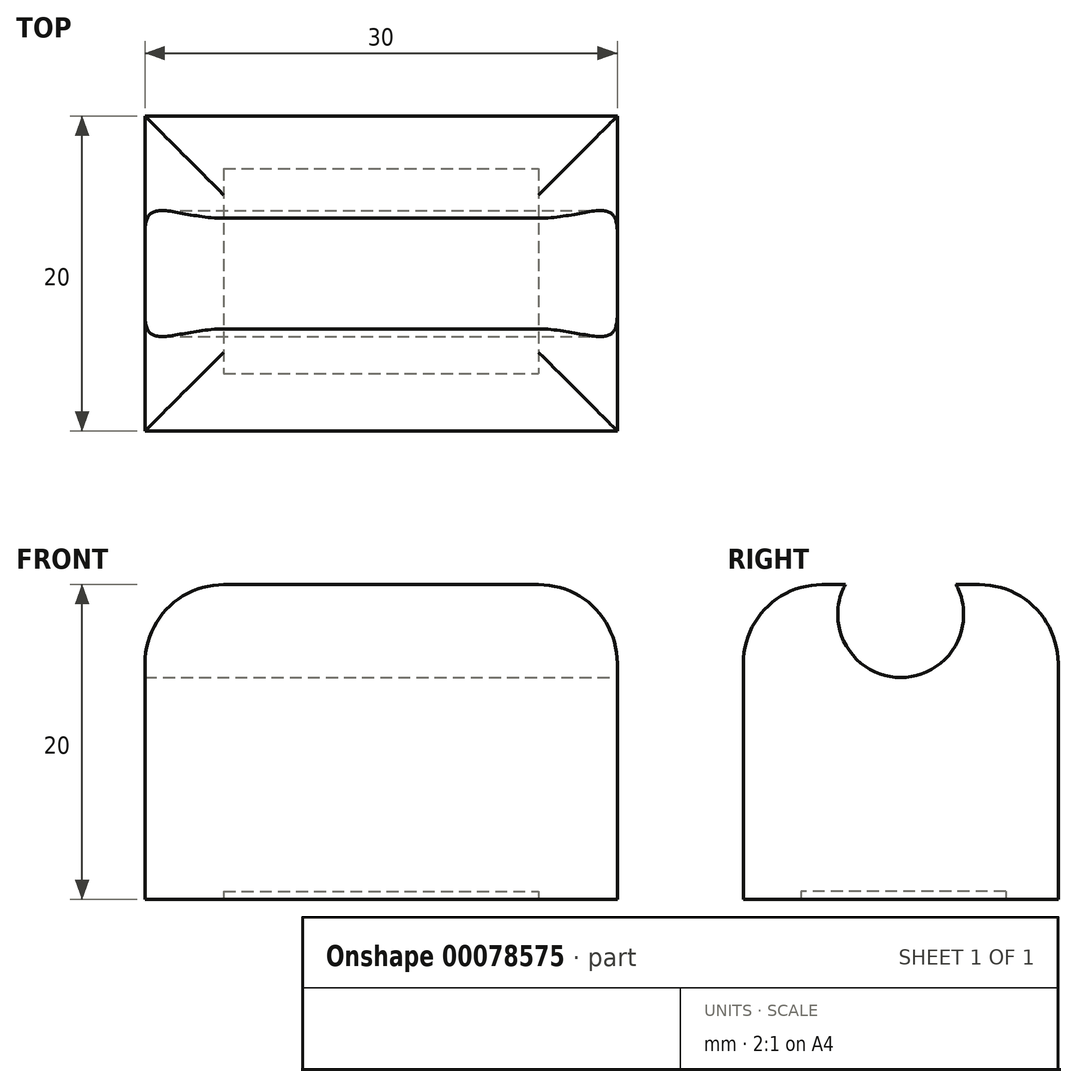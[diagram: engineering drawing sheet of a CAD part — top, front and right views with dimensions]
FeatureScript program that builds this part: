
annotation { "Feature Type Name" : "Feature", "Feature Type Description" : "" }
export const myFeature = defineFeature(function(context is Context, id is Id, definition is map)
    precondition{}
    {
        {
            var Q0;
            Q0=qCreatedBy(makeId("Right.planeOp"),FACE);
            var sketch = newSketch(context, id + "F0", { "sketchPlane" : qUnion([Q0])});
            skLineSegment(sketch, "E0", {"start": v(0, 0) * mm, "end": v(-20, 0) * mm});
            skLineSegment(sketch, "E1", {"start": v(-20, 0) * mm, "end": v(-20, 20) * mm});
            skLineSegment(sketch, "E2", {"start": v(-20, 20) * mm, "end": v(0, 20) * mm});
            skLineSegment(sketch, "E3", {"start": v(0, 20) * mm, "end": v(0, 0) * mm});
            skSolve(sketch);
        }
        {
            var Q0;
            Q0=makeQuery(id+"F0.imprint","IMPRINT",FACE,{"disambiguationData":[TD([[makeQuery(id+"F0.imprint","IMPRINT",EDGE,{"derivedFrom":sQuery(id+"F0.wireOp",EDGE,"E0")}),-1.0]])]});
            extrude(context, id + "F1", {"entities" : qUnion([Q0]), "depth" : 30 * mm});
        }
        {
            var Q0;
            Q0=makeQuery(id+"F1.opExtrude","CAP_FACE",FACE,{"disambiguationData":[OSD([sQuery(id+"F0.wireOp",EDGE,"E0"),sQuery(id+"F0.wireOp",EDGE,"E1"),sQuery(id+"F0.wireOp",EDGE,"E2"),sQuery(id+"F0.wireOp",EDGE,"E3")])],"isStart":false});
            var sketch = newSketch(context, id + "F2", { "sketchPlane" : qUnion([Q0])});
            skLineSegment(sketch, "E4", {"start": v(-20, 10) * mm, "end": v(0, 10) * mm, "construction": true});
            skLineSegment(sketch, "E5", {"start": v(-10, 20) * mm, "end": v(-10, 0) * mm, "construction": true});
            skLineSegment(sketch, "E6", {"start": v(-10, 0) * mm, "end": v(-20, 20) * mm, "construction": true});
            skLineSegment(sketch, "E7", {"start": v(-20, 20) * mm, "end": v(0, 10) * mm, "construction": true});
            skLineSegment(sketch, "E8", {"start": v(-15, 10) * mm, "end": v(0, 20) * mm, "construction": true});
            skLineSegment(sketch, "E9", {"start": v(0, 20) * mm, "end": v(-10, 0) * mm, "construction": true});
            skPoint(sketch, "E10", {"position": v(-10, 18.1) * mm});
            skSolve(sketch);
        }
        {
            var Q0;
            Q0=sQuery(id+"F2.wireOp",VERTEX,"1b50a934-3b71-4e1f-b5b8-8ca6462f1edd");
            var Q1;
            Q1=sQuery(id+"F2.wireOp",VERTEX,"E10");
            var Q2;
            Q2=makeQuery(id+"F1.opExtrude","SWEPT_BODY",BODY,{"disambiguationData":[OSD([sQuery(id+"F0.wireOp",EDGE,"E0"),sQuery(id+"F0.wireOp",EDGE,"E1"),sQuery(id+"F0.wireOp",EDGE,"E2"),sQuery(id+"F0.wireOp",EDGE,"E3")])]});
            hole(context, id + "F3", {"style" : HoleStyle.SIMPLE, "endStyle" : HoleEndStyle.BLIND, "holeDiameter" : 8 * mm, "holeDepth" : 50 * mm, "locations" : qUnion([Q0, Q1]), "scope" : qUnion([Q2])});
        }
        {
            var Q0;
            {var subQ0=sQuery(id+"F0.wireOp",EDGE,"E2");var subQ1=sQuery(id+"F0.wireOp",EDGE,"E1");Q0=makeQuery(id+"F3.hole-0.boolean.opBoolean","SPLIT",EDGE,{"disambiguationData":[TD([makeQuery(id+"F1.opExtrude","SWEPT_FACE",FACE,{"disambiguationData":[OSD([subQ1])]})])],"derivedFrom":makeQuery(id+"F1.opExtrude","CAP_EDGE",EDGE,{"disambiguationData":[OSD([subQ0])],"isStart":false})});}
            var Q1;
            Q1=makeQuery(id+"F1.opExtrude","SWEPT_EDGE",EDGE,{"disambiguationData":[OSD([sQuery(id+"F0.wireOp",EDGE,"E1"),sQuery(id+"F0.wireOp",EDGE,"E2")])]});
            var Q2;
            {var subQ0=sQuery(id+"F0.wireOp",EDGE,"E3");var subQ1=sQuery(id+"F0.wireOp",EDGE,"E2");Q2=makeQuery(id+"F3.hole-0.boolean.opBoolean","SPLIT",EDGE,{"disambiguationData":[TD([makeQuery(id+"F1.opExtrude","SWEPT_FACE",FACE,{"disambiguationData":[OSD([subQ0])]})])],"derivedFrom":makeQuery(id+"F1.opExtrude","CAP_EDGE",EDGE,{"disambiguationData":[OSD([subQ1])],"isStart":false})});}
            var Q3;
            Q3=makeQuery(id+"F1.opExtrude","SWEPT_EDGE",EDGE,{"disambiguationData":[OSD([sQuery(id+"F0.wireOp",EDGE,"E2"),sQuery(id+"F0.wireOp",EDGE,"E3")])]});
            var Q4;
            {var subQ0=sQuery(id+"F0.wireOp",EDGE,"E3");var subQ1=sQuery(id+"F0.wireOp",EDGE,"E2");Q4=makeQuery(id+"F3.hole-0.boolean.opBoolean","SPLIT",EDGE,{"disambiguationData":[TD([makeQuery(id+"F1.opExtrude","SWEPT_FACE",FACE,{"disambiguationData":[OSD([subQ0])]})])],"derivedFrom":makeQuery(id+"F1.opExtrude","CAP_EDGE",EDGE,{"disambiguationData":[OSD([subQ1])],"isStart":true})});}
            var Q5;
            {var subQ0=sQuery(id+"F0.wireOp",EDGE,"E2");var subQ1=sQuery(id+"F0.wireOp",EDGE,"E1");Q5=makeQuery(id+"F3.hole-0.boolean.opBoolean","SPLIT",EDGE,{"disambiguationData":[TD([makeQuery(id+"F1.opExtrude","SWEPT_FACE",FACE,{"disambiguationData":[OSD([subQ1])]})])],"derivedFrom":makeQuery(id+"F1.opExtrude","CAP_EDGE",EDGE,{"disambiguationData":[OSD([subQ0])],"isStart":true})});}
            fillet(context, id + "F4", {"entities" : qUnion([Q0, Q1, Q2, Q3, Q4, Q5]), "radius" : 5 * mm, "tangentPropagation" : true, "allowEdgeOverflow" : false});
        }
        {
            var Q0;
            Q0=makeQuery(id+"F1.opExtrude","SWEPT_FACE",FACE,{"disambiguationData":[OSD([sQuery(id+"F0.wireOp",EDGE,"E0")])]});
            var sketch = newSketch(context, id + "F5", { "sketchPlane" : qUnion([Q0])});
            skLineSegment(sketch, "E11.bottom", {"start": v(5, 3.33) * mm, "end": v(25, 3.33) * mm});
            skLineSegment(sketch, "E11.top", {"start": v(5, 16.33) * mm, "end": v(25, 16.33) * mm});
            skLineSegment(sketch, "E11.left", {"start": v(5, 3.33) * mm, "end": v(5, 16.33) * mm});
            skLineSegment(sketch, "E11.right", {"start": v(25, 3.33) * mm, "end": v(25, 16.33) * mm});
            skPoint(sketch, "E11.middle", {"position": v(15, 9.83) * mm});
            skSolve(sketch);
        }
        {
            var Q0;
            Q0 = qSketchRegion(id + "F5", true);
            extrude(context, id + "F6", {"entities" : qUnion([Q0]), "operationType" : NewBodyOperationType.REMOVE, "oppositeDirection" : true, "depth" : 0.5 * mm});
        }
    });
